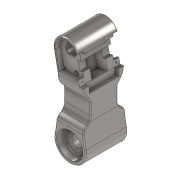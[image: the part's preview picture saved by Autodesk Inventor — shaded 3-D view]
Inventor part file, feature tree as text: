
AUTODESK INVENTOR PART (.ipt)
format: ipt  version: 2020.3 (Build 243373010, 373A)  size: 822,272 bytes
history: native  units: mm
features: sketch x33, extrude x19, projected_geometry x11, fillet x5, mirror x4, chamfer x4, hole x3, plane x2, other x2, delete_face x1, revolve x1
ambient origin geometry x8: Origin, YZ Plane, XZ Plane, XY Plane, X Axis, Y Axis, Z Axis, Center Point
bodies: Body1 (feature_tree)
feature tree (85):
  extrude  "Extrusion8"  Depth=48.0mm
  extrude  "Extrusion12"  Depth=120.0mm
  extrude  "Extrusion15"  Depth=50.0mm
  extrude  "Extrusion16"  Depth=185.0mm
  extrude  "Extrusion17"  Depth=65.0mm
  fillet  "Fillet16"  Radius=190.0mm
  fillet  "Fillet17"  Radius=15.0mm
  extrude  "Extrusion19"  Depth=65.0mm
  extrude  "Extrusion20"  Depth=125.0mm TaperAngle=0.0deg
  extrude  "Extrusion21"  Depth=10.0mm
  extrude  "Extrusion22"  Depth=20.0mm TaperAngle=0.0deg
  delete_face  "Delete Face1"
  mirror  "Mirror4"
  extrude  "Extrusion23"  Depth=20.0mm TaperAngle=0.0deg
  extrude  "Extrusion25"  Depth=25.0mm TaperAngle=0.0deg
  hole  "Hole1"  [1 undecoded]
  mirror  "Mirror5"
  sketch  "Sketch41"  dims[d180=85.0mm d181=50.0mm d182=0.0mm]
  extrude  "Extrusion26"  Depth=50.0mm TaperAngle=0.0deg
  mirror  "Mirror6"
  hole  "Hole3"  [1 undecoded]
  fillet  "Fillet20"  Radius=7.0mm
  chamfer  "Chamfer4"  Distance=12.5mm
  chamfer  "Chamfer5"  Distance=25.0mm
  extrude  "Extrusion27"  Depth=25.0mm
  sketch  "Sketch45"  dims[d196=7.0mm]
  extrude  "Extrusion29"  Depth=10.0mm
  fillet  "Fillet21"  Radius=13.948976mm
  fillet  "Fillet22"  Radius=2.0mm
  sketch  "Sketch54"  dims[d198=92.5mm]
  sketch  "Sketch55"  dims[d199=6.917mm d200=16.0mm d201=18.0mm d202=4.8mm d203=90.0deg d204=21.1mm d205=0.0mm]
  sketch  "Sketch56"  dims[d206=80.0mm]
  sketch  "Sketch59"  dims[d207=40.0mm]
  extrude  "Extrusion30"  Depth=10.0mm TaperAngle=45.0deg
  mirror  "Mirror9"
  chamfer  "Chamfer8"  Distance=2.0mm Angle=45.0deg
  sketch  "Sketch61"  dims[d214=12.0mm]
  extrude  "Extrusion33"  Depth=10.0mm TaperAngle=0.0deg
  chamfer  "Chamfer10"  Distance=15.0mm
  sketch  "Sketch66"  dims[d216=20.0mm]
  plane  "Work Plane9"
  other  "Work Axis1"
  other  "Work Axis2"
  plane  "Work Plane10"
  revolve  "Revolution4"  [1 undecoded]
  extrude  "Extrusion38"  Depth=10.0mm
  sketch  "Sketch74"  dims[d229=160.0mm]
  extrude  "Extrusion39"  Depth=35.0mm TaperAngle=0.0deg
  sketch  "Sketch76"  dims[d231=15.0mm]
  hole  "Hole4"  [1 undecoded]
  extrude  "Extrusion40"  Depth=5.0mm
  sketch  "Sketch16"  dims[d64=150.0mm d65=48.0mm]
  sketch  "Sketch21"  dims[d66=198.0mm d67=0.0mm d117=120.0mm]
  sketch  "Sketch24"  dims[d118=190.0mm d119=0.0mm d144=50.0mm]
  sketch  "Sketch27"  dims[d145=4.0mm d146=0.0mm d147=185.0mm]
  projected_geometry  "Projected Loop11"
  projected_geometry  "Projected Loop12"
  sketch  "Sketch28"  dims[d148=65.0mm d149=65.0mm d150=190.0mm d151=15.0mm]
  projected_geometry  "Projected Loop13"
  sketch  "Sketch32"  dims[d152=45.0mm d153=65.0mm]
  sketch  "Sketch33"  dims[d154=25.0mm d155=125.0mm d156=0.0mm]
  sketch  "Sketch34"  dims[d157=10.0mm d158=0.0mm d159=425.0mm]
  projected_geometry  "Projected Loop15"
  sketch  "Sketch35"  dims[d160=481.0mm d169=20.0mm d170=0.0mm]
  projected_geometry  "Projected Loop16"
  sketch  "Sketch36"  dims[d171=190.0mm d172=20.0mm d173=0.0mm]
  sketch  "Sketch39"  dims[d174=10.0mm d175=25.0mm d176=0.0mm]
  projected_geometry  "Projected Loop17"
  projected_geometry  "Projected Loop18"
  sketch  "Sketch40"  dims[d177=189.555mm d178=0.0mm d179=75.0mm]
  sketch  "Sketch42"  dims[d189=10.0mm d190=0.0mm d191=5.0mm d193=7.0mm]
  sketch  "Sketch43"  dims[d194=5.0mm]
  sketch  "Sketch44"  dims[d195=7.0mm]
  projected_geometry  "Projected Loop19"
  sketch  "Sketch46"  dims[d197=14.0mm]
  projected_geometry  "Projected Loop22"
  projected_geometry  "Projected Loop24"
  sketch  "Sketch60"  dims[d213=12.0mm]
  sketch  "Sketch65"  dims[d215=40.0mm]
  projected_geometry  "Projected Loop27"
  sketch  "Sketch72"  dims[d217=15.0mm d218=12.5mm d219=0.0mm]
  sketch  "Sketch73"  dims[d228=95.0mm]
  sketch  "Sketch75"  dims[d230=90.0mm]
  sketch  "Sketch77"  dims[d232=15.0mm]
  sketch  "Sketch78"  dims[d233=13.0mm d234=25.0mm d235=25.0mm d236=12.330008mm d237=13.948976mm d238=6.917mm d239=8.0mm d240=18.0mm d241=4.8mm d242=90.0deg d243=10.0mm d244=0.0mm d249=2.0mm d250=2.0mm d251=2.0mm d252=45.0deg d253=2.0mm d254=2.0mm d255=45.0deg d256=10.0mm d257=0.0mm d258=15.0mm d260=5.0mm d265=100.0mm d266=35.0mm d267=0.0mm d271=2.0mm d272=5.0mm d282=25.0mm d283=25.0mm d284=121.278985mm d285=140.0mm d288=120.0mm d289=26.025mm d290=0.0mm d291=2.0mm d292=2.0mm d293=45.0deg d294=25.0mm d302=10.0mm d303=0.0mm d304=5.0mm d305=2.0mm d306=45.0deg d307=32.5mm d324=6.0mm d325=0.0mm d328=90.0deg d329=20.0mm d330=20.0mm d331=15.0mm d332=0.0mm d333=48.55mm d334=20.0mm d335=100.0mm d336=0.0mm d337=0.0mm d338=57.0mm d339=4.134mm d340=10.0mm d341=4.0mm d342=2.0mm d343=90.0deg d344=14.2mm d345=20.594885mm d346=58.0mm d347=124.008mm d348=0.0mm d68=0.5mm d69=0.872665mm d295=0.5mm d296=0.872665mm d297=0.5mm d298=0.872665mm d316=0.5mm d317=0.872665mm d318=0.5mm d319=0.872665mm]
note: 4 required parameter values undecoded (feature->parameter linkage not recoverable at this tier; creation-order binding heuristic only, values carry confidence <= 0.55)